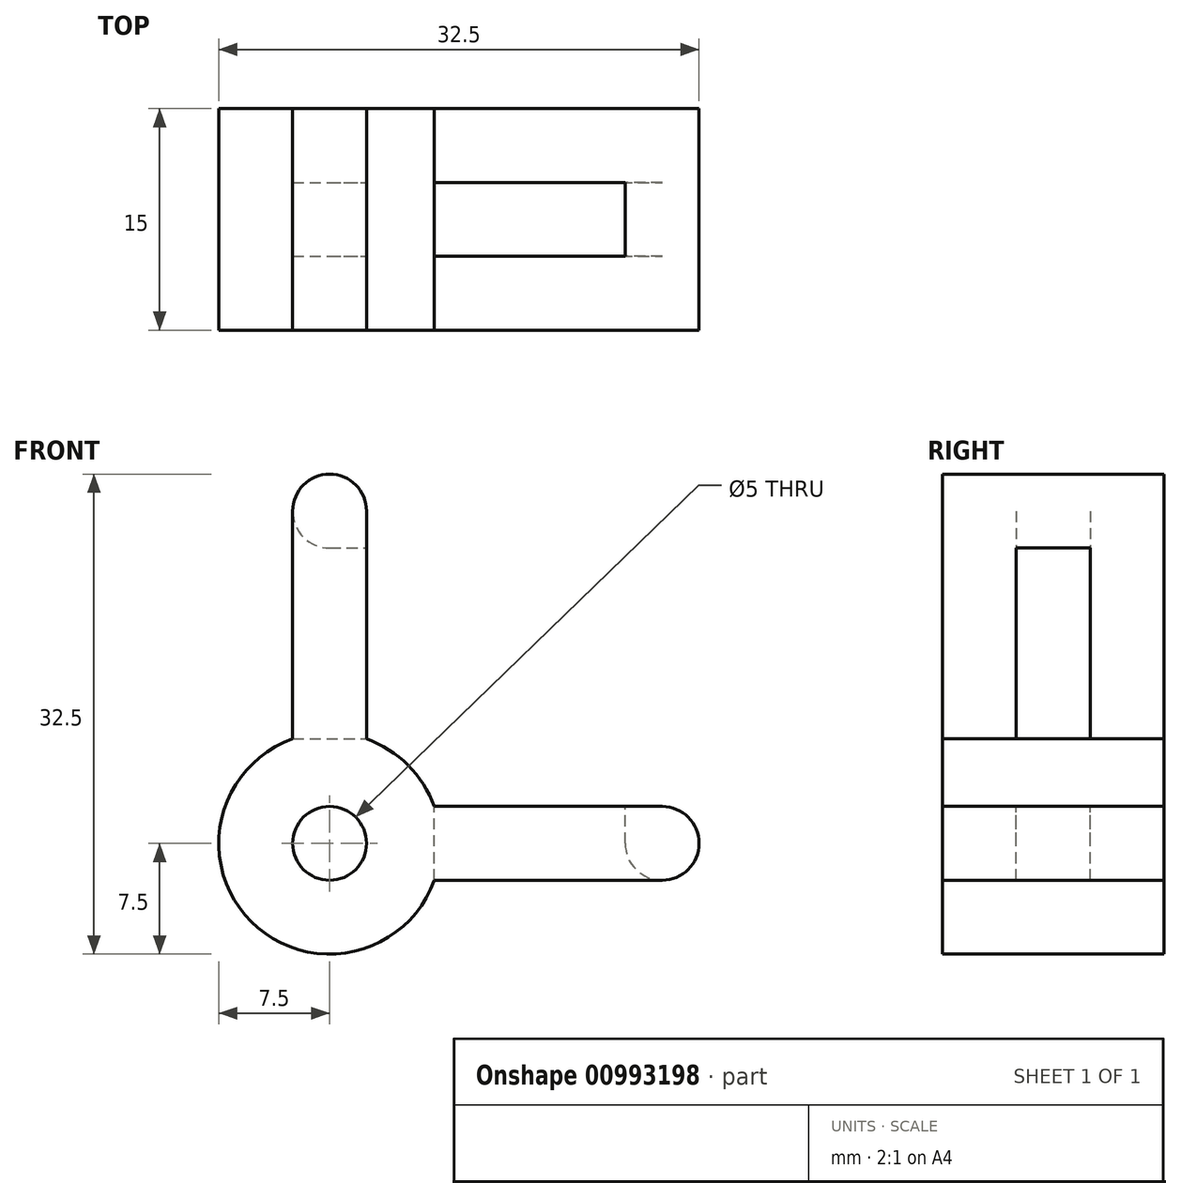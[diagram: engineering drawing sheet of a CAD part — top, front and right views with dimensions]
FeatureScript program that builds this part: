
annotation { "Feature Type Name" : "Feature", "Feature Type Description" : "" }
export const myFeature = defineFeature(function(context is Context, id is Id, definition is map)
    precondition{}
    {
        {
            var Q0;
            Q0=qCreatedBy(makeId("Front.planeOp"),FACE);
            var sketch = newSketch(context, id + "F0", { "sketchPlane" : qUnion([Q0])});
            skLineSegment(sketch, "E0.bottom", {"start": v(-2.5, 25) * mm, "end": v(2.5, 25) * mm});
            skLineSegment(sketch, "E0.left", {"start": v(-2.5, 25) * mm, "end": v(-2.5, 7.07) * mm});
            skLineSegment(sketch, "E0.right", {"start": v(2.5, 25) * mm, "end": v(2.5, 7.07) * mm});
            skLineSegment(sketch, "E1.bottom", {"start": v(25, 2.5) * mm, "end": v(7.07, 2.5) * mm});
            skLineSegment(sketch, "E1.top", {"start": v(25, -2.5) * mm, "end": v(7.07, -2.5) * mm});
            skLineSegment(sketch, "E1.left", {"start": v(25, 2.5) * mm, "end": v(25, -2.5) * mm});
            skLineSegment(sketch, "E2", {"start": v(0, 0) * mm, "end": v(25, 0) * mm, "construction": true});
            skArc(sketch, "E3", {"start": v(-2.5, 7.07) * mm, "mid": v(-5.3, -5.3) * mm, "end": v(7.07, -2.5) * mm});
            skPoint(sketch, "E4", {"position": v(0, 25) * mm});
            skArc(sketch, "E5.trimOffspring", {"start": v(7.07, 2.5) * mm, "mid": v(5.3, 5.3) * mm, "end": v(2.5, 7.07) * mm});
            skSolve(sketch);
        }
        {
            var Q0;
            Q0 = qSketchRegion(id + "F0", true);
            extrude(context, id + "F1", {"entities" : qUnion([Q0]), "depth" : 15 * mm, "offsetDistance" : 25 * mm});
        }
        {
            var Q0;
            Q0=makeQuery(id+"F1.opExtrude","SWEPT_FACE",FACE,{"disambiguationData":[OSD([sQuery(id+"F0.wireOp",EDGE,"E0.right")])]});
            var sketch = newSketch(context, id + "F2", { "sketchPlane" : qUnion([Q0])});
            skLineSegment(sketch, "E6.bottom", {"start": v(-10, 20) * mm, "end": v(-5, 20) * mm});
            skLineSegment(sketch, "E6.top", {"start": v(-10, 7.07) * mm, "end": v(-5, 7.07) * mm});
            skLineSegment(sketch, "E6.left", {"start": v(-10, 20) * mm, "end": v(-10, 7.07) * mm});
            skLineSegment(sketch, "E6.right", {"start": v(-5, 20) * mm, "end": v(-5, 7.07) * mm});
            skSolve(sketch);
        }
        {
            var Q0;
            Q0 = qSketchRegion(id + "F2", true);
            extrude(context, id + "F3", {"entities" : qUnion([Q0]), "operationType" : NewBodyOperationType.REMOVE, "oppositeDirection" : true, "depth" : 25 * mm, "offsetDistance" : 25 * mm});
        }
        {
            var Q0;
            Q0=makeQuery(id+"F1.opExtrude","SWEPT_FACE",FACE,{"disambiguationData":[OSD([sQuery(id+"F0.wireOp",EDGE,"E1.bottom")])]});
            var sketch = newSketch(context, id + "F4", { "sketchPlane" : qUnion([Q0])});
            skLineSegment(sketch, "E7.bottom", {"start": v(20, -5) * mm, "end": v(7.07, -5) * mm});
            skLineSegment(sketch, "E7.top", {"start": v(20, -10) * mm, "end": v(7.07, -10) * mm});
            skLineSegment(sketch, "E7.left", {"start": v(20, -5) * mm, "end": v(20, -10) * mm});
            skLineSegment(sketch, "E7.right", {"start": v(7.07, -5) * mm, "end": v(7.07, -10) * mm});
            skSolve(sketch);
        }
        {
            var Q0;
            Q0 = qSketchRegion(id + "F4", true);
            extrude(context, id + "F5", {"entities" : qUnion([Q0]), "operationType" : NewBodyOperationType.REMOVE, "oppositeDirection" : true, "depth" : 25 * mm, "offsetDistance" : 25 * mm});
        }
        {
            var Q0;
            Q0=makeQuery(id+"F1.opExtrude","SWEPT_EDGE",EDGE,{"disambiguationData":[OSD([sQuery(id+"F0.wireOp",EDGE,"E0.bottom"),sQuery(id+"F0.wireOp",EDGE,"E0.left")])]});
            var Q1;
            Q1=makeQuery(id+"F1.opExtrude","SWEPT_EDGE",EDGE,{"disambiguationData":[OSD([sQuery(id+"F0.wireOp",EDGE,"E0.bottom"),sQuery(id+"F0.wireOp",EDGE,"E0.right")])]});
            var Q2;
            Q2=makeQuery(id+"F3.boolean.opBoolean","INTERSECT",EDGE,{"derivedFrom":[makeQuery(id+"F1.opExtrude","SWEPT_FACE",FACE,{"disambiguationData":[OSD([sQuery(id+"F0.wireOp",EDGE,"E0.left")])]}),makeQuery(id+"F3.opExtrude","SWEPT_FACE",FACE,{"disambiguationData":[OSD([sQuery(id+"F2.wireOp",EDGE,"E6.bottom")])]})]});
            var Q3;
            Q3=makeQuery(id+"F3.boolean.opBoolean","COPY",EDGE,{"derivedFrom":makeQuery(id+"F3.opExtrude","CAP_EDGE",EDGE,{"disambiguationData":[OSD([sQuery(id+"F2.wireOp",EDGE,"E6.bottom")])],"isStart":true})});
            var Q4;
            Q4=makeQuery(id+"F1.opExtrude","SWEPT_EDGE",EDGE,{"disambiguationData":[OSD([sQuery(id+"F0.wireOp",EDGE,"E1.top"),sQuery(id+"F0.wireOp",EDGE,"E1.left")])]});
            var Q5;
            Q5=makeQuery(id+"F1.opExtrude","SWEPT_EDGE",EDGE,{"disambiguationData":[OSD([sQuery(id+"F0.wireOp",EDGE,"E1.bottom"),sQuery(id+"F0.wireOp",EDGE,"E1.left")])]});
            var Q6;
            Q6=makeQuery(id+"F5.boolean.opBoolean","INTERSECT",EDGE,{"derivedFrom":[makeQuery(id+"F1.opExtrude","SWEPT_FACE",FACE,{"disambiguationData":[OSD([sQuery(id+"F0.wireOp",EDGE,"E1.top")])]}),makeQuery(id+"F5.opExtrude","SWEPT_FACE",FACE,{"disambiguationData":[OSD([sQuery(id+"F4.wireOp",EDGE,"E7.left")])]})]});
            var Q7;
            Q7=makeQuery(id+"F5.boolean.opBoolean","COPY",EDGE,{"derivedFrom":makeQuery(id+"F5.opExtrude","CAP_EDGE",EDGE,{"disambiguationData":[OSD([sQuery(id+"F4.wireOp",EDGE,"E7.left")])],"isStart":true})});
            fillet(context, id + "F6", {"entities" : qUnion([Q0, Q1, Q2, Q3, Q4, Q5, Q6, Q7]), "radius" : 2.5 * mm, "tangentPropagation" : true, "allowEdgeOverflow" : false});
        }
        {
            var Q0;
            Q0=makeQuery(id+"F1.opExtrude","CAP_FACE",FACE,{"disambiguationData":[OSD([sQuery(id+"F0.wireOp",EDGE,"E0.bottom"),sQuery(id+"F0.wireOp",EDGE,"E0.left"),sQuery(id+"F0.wireOp",EDGE,"E0.right"),sQuery(id+"F0.wireOp",EDGE,"E1.bottom"),sQuery(id+"F0.wireOp",EDGE,"E1.top"),sQuery(id+"F0.wireOp",EDGE,"E1.left"),sQuery(id+"F0.wireOp",EDGE,"E3"),sQuery(id+"F0.wireOp",EDGE,"E5.trimOffspring")])],"isStart":false});
            var sketch = newSketch(context, id + "F7", { "sketchPlane" : qUnion([Q0])});
            skCircle(sketch, "E8", {"center": v(0, 0) * mm, "radius": 2.5 * mm});
            skSolve(sketch);
        }
        {
            var Q0;
            Q0 = qSketchRegion(id + "F7", true);
            extrude(context, id + "F8", {"entities" : qUnion([Q0]), "operationType" : NewBodyOperationType.REMOVE, "oppositeDirection" : true, "depth" : 25 * mm, "offsetDistance" : 25 * mm});
        }
    });
